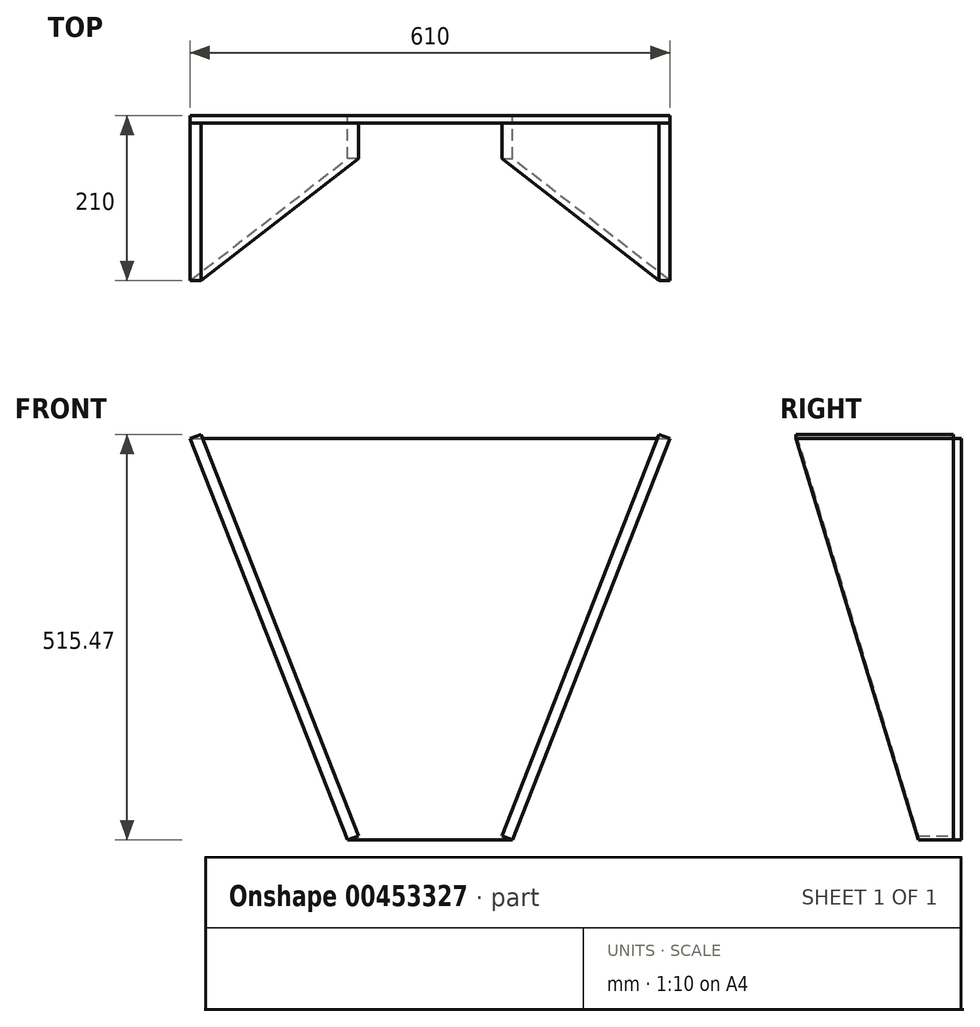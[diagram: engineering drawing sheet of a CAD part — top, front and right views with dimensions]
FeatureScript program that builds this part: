
annotation { "Feature Type Name" : "Feature", "Feature Type Description" : "" }
export const myFeature = defineFeature(function(context is Context, id is Id, definition is map)
    precondition{}
    {
        {
            var Q0;
            Q0=qCreatedBy(makeId("Front.planeOp"),FACE);
            var sketch = newSketch(context, id + "F0", { "sketchPlane" : qUnion([Q0])});
            skLineSegment(sketch, "E0", {"start": v(-305, 221.77) * mm, "end": v(305, 221.77) * mm});
            skLineSegment(sketch, "E1", {"start": v(305, 221.77) * mm, "end": v(105, -288.23) * mm});
            skLineSegment(sketch, "E2", {"start": v(105, -288.23) * mm, "end": v(-105, -288.23) * mm});
            skLineSegment(sketch, "E3", {"start": v(-105, -288.23) * mm, "end": v(-305, 221.77) * mm});
            skPoint(sketch, "E4", {"position": v(0, 221.77) * mm});
            skPoint(sketch, "E5", {"position": v(0, -288.23) * mm});
            skSolve(sketch);
        }
        {
            var Q0;
            Q0 = qSketchRegion(id + "F0", true);
            extrude(context, id + "F1", {"entities" : qUnion([Q0]), "depth" : 10 * mm});
        }
        {
            var Q0;
            Q0=makeQuery(id+"F1.opExtrude","SWEPT_FACE",FACE,{"disambiguationData":[OSD([sQuery(id+"F0.wireOp",EDGE,"E3")])]});
            var sketch = newSketch(context, id + "F2", { "sketchPlane" : qUnion([Q0])});
            skLineSegment(sketch, "E6", {"start": v(10, 317.81) * mm, "end": v(210, 317.81) * mm});
            skLineSegment(sketch, "E7", {"start": v(210, 317.81) * mm, "end": v(55, -230) * mm});
            skLineSegment(sketch, "E8", {"start": v(55, -230) * mm, "end": v(10, -230) * mm});
            skLineSegment(sketch, "E9", {"start": v(10, -230) * mm, "end": v(10, 317.81) * mm});
            skSolve(sketch);
        }
        {
            var Q0;
            Q0=makeQuery(id+"F2.imprint","IMPRINT",FACE,{"disambiguationData":[TD([[makeQuery(id+"F2.imprint","IMPRINT",EDGE,{"derivedFrom":sQuery(id+"F2.wireOp",EDGE,"E6")}),-1.0]])]});
            extrude(context, id + "F3", {"entities" : qUnion([Q0]), "oppositeDirection" : true, "depth" : 15 * mm});
        }
        {
            var Q0;
            Q0=makeQuery(id+"F3.opExtrude","SWEPT_BODY",BODY,{"disambiguationData":[OSD([sQuery(id+"F2.wireOp",EDGE,"E6"),sQuery(id+"F2.wireOp",EDGE,"E7"),sQuery(id+"F2.wireOp",EDGE,"E8"),sQuery(id+"F2.wireOp",EDGE,"E9")])]});
            var Q1;
            Q1=qCreatedBy(makeId("Right.planeOp"),FACE);
            mirror(context, id + "F4", {"entities" : qUnion([Q0]), "mirrorPlane" : qUnion([Q1])});
        }
    });
